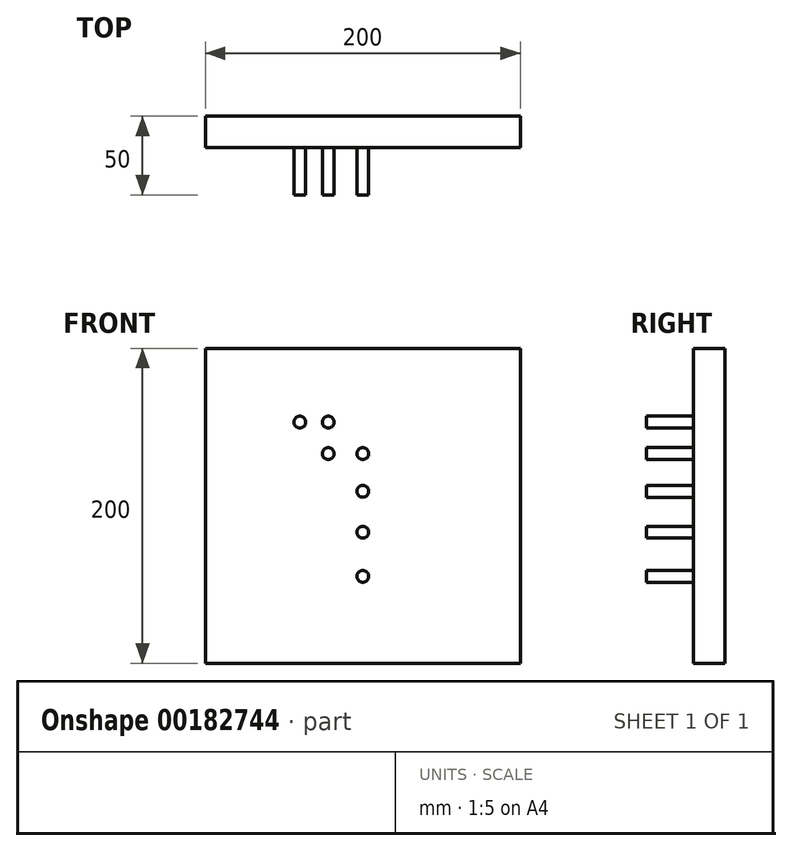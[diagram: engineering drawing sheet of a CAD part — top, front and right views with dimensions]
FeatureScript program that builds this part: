
annotation { "Feature Type Name" : "Feature", "Feature Type Description" : "" }
export const myFeature = defineFeature(function(context is Context, id is Id, definition is map)
    precondition{}
    {
        {
            var Q0;
            Q0=qCreatedBy(makeId("Front.planeOp"),FACE);
            var sketch = newSketch(context, id + "F0", { "sketchPlane" : qUnion([Q0])});
            skLineSegment(sketch, "E0.bottom", {"start": v(100, 100) * mm, "end": v(-100, 100) * mm});
            skLineSegment(sketch, "E0.top", {"start": v(100, -100) * mm, "end": v(-100, -100) * mm});
            skLineSegment(sketch, "E0.left", {"start": v(100, 100) * mm, "end": v(100, -100) * mm});
            skLineSegment(sketch, "E0.right", {"start": v(-100, 100) * mm, "end": v(-100, -100) * mm});
            skPoint(sketch, "E0.middle", {"position": v(0, 0) * mm});
            skSolve(sketch);
        }
        {
            var Q0;
            Q0=makeQuery(id+"F0.imprint","IMPRINT",FACE,{"disambiguationData":[TD([[makeQuery(id+"F0.imprint","IMPRINT",EDGE,{"derivedFrom":sQuery(id+"F0.wireOp",EDGE,"E0.bottom")}),1.0]])]});
            extrude(context, id + "F1", {"entities" : qUnion([Q0]), "depth" : 20 * mm});
        }
        {
            var Q0;
            Q0=makeQuery(id+"F1.opExtrude","CAP_FACE",FACE,{"disambiguationData":[OSD([sQuery(id+"F0.wireOp",EDGE,"E0.bottom"),sQuery(id+"F0.wireOp",EDGE,"E0.top"),sQuery(id+"F0.wireOp",EDGE,"E0.left"),sQuery(id+"F0.wireOp",EDGE,"E0.right")])],"isStart":false});
            var sketch = newSketch(context, id + "F2", { "sketchPlane" : qUnion([Q0])});
            skCircle(sketch, "E1", {"center": v(-40, 53.21) * mm, "radius": 3.75 * mm});
            skCircle(sketch, "E2", {"center": v(-22, 53.21) * mm, "radius": 3.75 * mm});
            skCircle(sketch, "E3", {"center": v(-22, 33.21) * mm, "radius": 3.75 * mm});
            skCircle(sketch, "E4", {"center": v(0, 33.21) * mm, "radius": 3.75 * mm});
            skCircle(sketch, "E5", {"center": v(0, 9.21) * mm, "radius": 3.75 * mm});
            skCircle(sketch, "E6", {"center": v(0, -16.79) * mm, "radius": 3.75 * mm});
            skCircle(sketch, "E7", {"center": v(0, -44.79) * mm, "radius": 3.75 * mm});
            skSolve(sketch);
        }
        {
            var Q0;
            Q0 = qSketchRegion(id + "F2", true);
            extrude(context, id + "F3", {"entities" : qUnion([Q0]), "operationType" : NewBodyOperationType.ADD, "depth" : 30 * mm});
        }
    });
